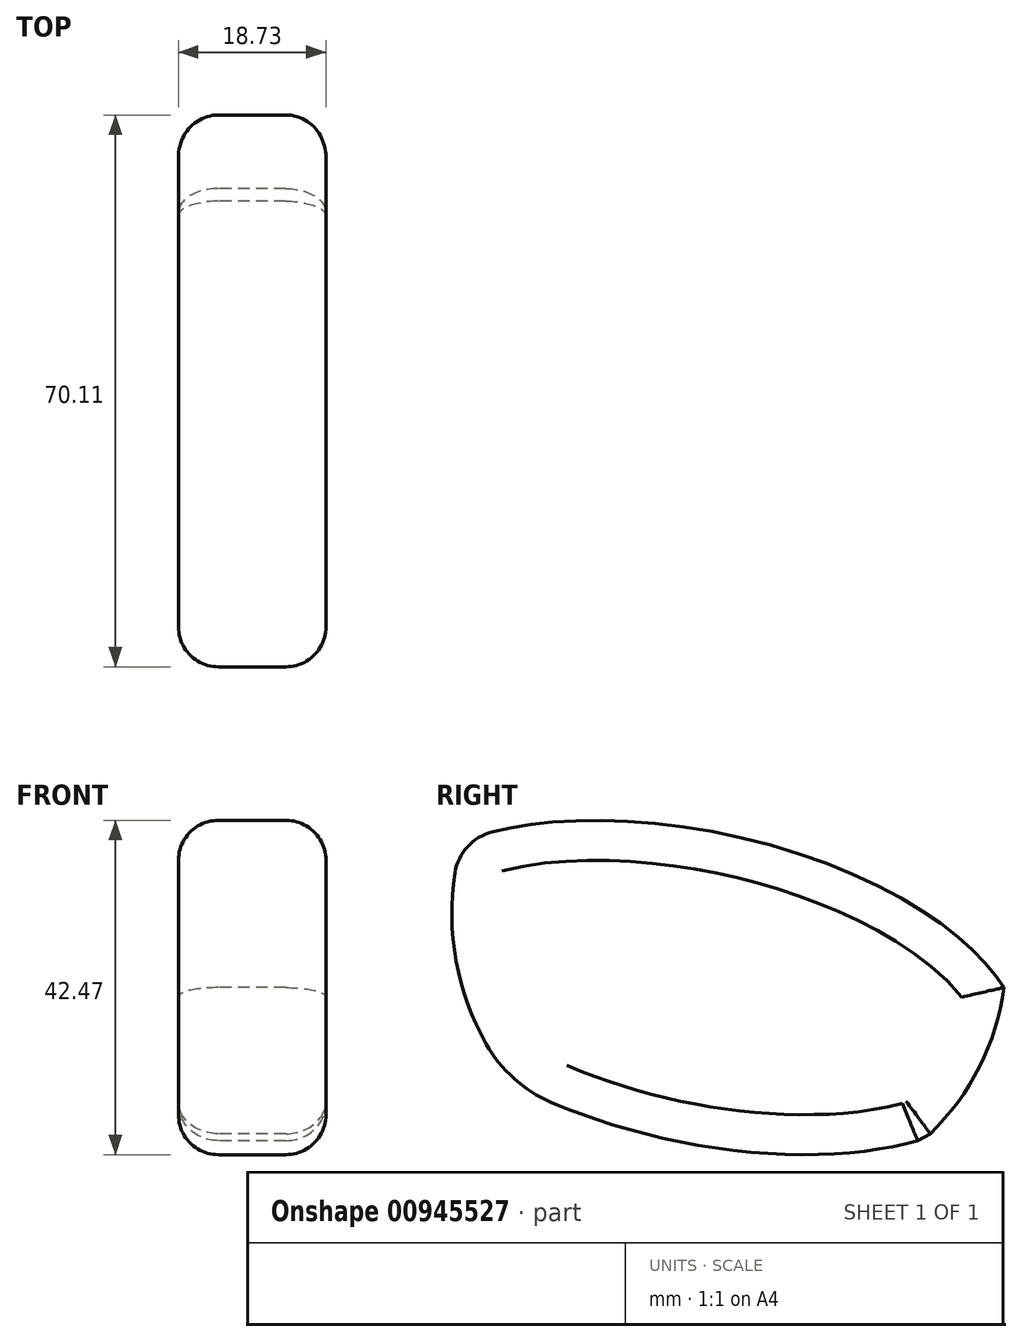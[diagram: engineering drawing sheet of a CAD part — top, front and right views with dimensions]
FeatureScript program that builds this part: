
annotation { "Feature Type Name" : "Feature", "Feature Type Description" : "" }
export const myFeature = defineFeature(function(context is Context, id is Id, definition is map)
    precondition{}
    {
        {
            var Q0;
            Q0=qCreatedBy(makeId("Right.planeOp"),FACE);
            var sketch = newSketch(context, id + "F0", { "sketchPlane" : qUnion([Q0])});
            skEllipticalArc(sketch, "E0", {});
            skArc(sketch, "E1", {"start": v(-67.19, 43.39) * mm, "mid": v(-67.04, 32.18) * mm, "end": v(-63.23, 21.65) * mm});
            skPoint(sketch, "E2.visualSharp", {"position": v(-59.6, 16.42) * mm});
            skArc(sketch, "E2.filletArc", {"start": v(-63.23, 21.65) * mm, "mid": v(-59.71, 17.27) * mm, "end": v(-54.97, 14.24) * mm});
            skEllipticalArc(sketch, "E3.trimOffspring", {});
            skPoint(sketch, "E4.visualSharp", {"position": v(0, 32.1) * mm});
            skPoint(sketch, "E5.visualSharp", {"position": v(-10.12, 8.92) * mm});
            skArc(sketch, "E6", {"start": v(-6.83, 10.24) * mm, "mid": v(-0.57, 18.72) * mm, "end": v(2.52, 28.8) * mm});
            skPoint(sketch, "E7.visualSharp", {"position": v(-66.32, 47.37) * mm});
            skArc(sketch, "E7.filletArc", {"start": v(-62.46, 48.57) * mm, "mid": v(-65.6, 46.69) * mm, "end": v(-67.19, 43.39) * mm});
            skLineSegment(sketch, "E8", {"start": v(-8.43, 9.36) * mm, "end": v(-6.83, 10.24) * mm});
            const initialGuessF0  = {"E0": [-0.036014964049215066, 0.028814417792441746, 0.9764174041222506, -0.21589129886858693, 0.0414924682048282, 0.019720746164997183, 4.3330950452189825, 5.5609774550021775], "E3.trimOffspring": [-0.036014964049215066, 0.028814417792441746, 0.9764174041222506, -0.21589129886858693, 0.0414924682048282, 0.019720746164997183, 0.43503496477957754, 2.3821123687809824]};
            skSetInitialGuess(sketch, initialGuessF0);
            skSolve(sketch);
        }
        {
            var Q0;
            Q0=qCreatedBy(makeId("Front.planeOp"),FACE);
            var sketch = newSketch(context, id + "F1", { "sketchPlane" : qUnion([Q0])});
            skLineSegment(sketch, "E9", {"start": v(-18.75, 37) * mm, "end": v(-37.48, 37) * mm});
            skSolve(sketch);
        }
        {
            var Q0;
            Q0=makeQuery(id+"F0.imprint","IMPRINT",FACE,{"disambiguationData":[TD([[makeQuery(id+"F0.imprint","IMPRINT",EDGE,{"derivedFrom":sQuery(id+"F0.wireOp",EDGE,"E0")}),1.0]])]});
            var Q1;
            Q1=sQuery(id+"F1.wireOp",EDGE,"E9");
            sweep(context, id + "F2", {"profiles" : qUnion([Q0]), "path" : qUnion([Q1])});
        }
        {
            var Q0;
            Q0=makeQuery(id+"F2.opSweep","CAP_FACE",FACE,{"disambiguationData":[OSD([sQuery(id+"F0.wireOp",EDGE,"E0"),sQuery(id+"F0.wireOp",EDGE,"E1"),sQuery(id+"F0.wireOp",EDGE,"E2.filletArc"),sQuery(id+"F0.wireOp",EDGE,"E3.trimOffspring"),sQuery(id+"F0.wireOp",EDGE,"E6"),sQuery(id+"F0.wireOp",EDGE,"E7.filletArc"),sQuery(id+"F0.wireOp",EDGE,"E8"),sQuery(id+"F1.wireOp",VERTEX,"E9.start")])],"isStart":true});
            var Q1;
            Q1=makeQuery(id+"F2.opSweep","CAP_FACE",FACE,{"disambiguationData":[OSD([sQuery(id+"F0.wireOp",EDGE,"E0"),sQuery(id+"F0.wireOp",EDGE,"E1"),sQuery(id+"F0.wireOp",EDGE,"E2.filletArc"),sQuery(id+"F0.wireOp",EDGE,"E3.trimOffspring"),sQuery(id+"F0.wireOp",EDGE,"E6"),sQuery(id+"F0.wireOp",EDGE,"E7.filletArc"),sQuery(id+"F0.wireOp",EDGE,"E8"),sQuery(id+"F1.wireOp",VERTEX,"E9.end")])],"isStart":false});
            fillet(context, id + "F3", {"entities" : qUnion([Q0, Q1]), "radius" : 5.08 * mm, "tangentPropagation" : true, "allowEdgeOverflow" : false});
        }
    });
